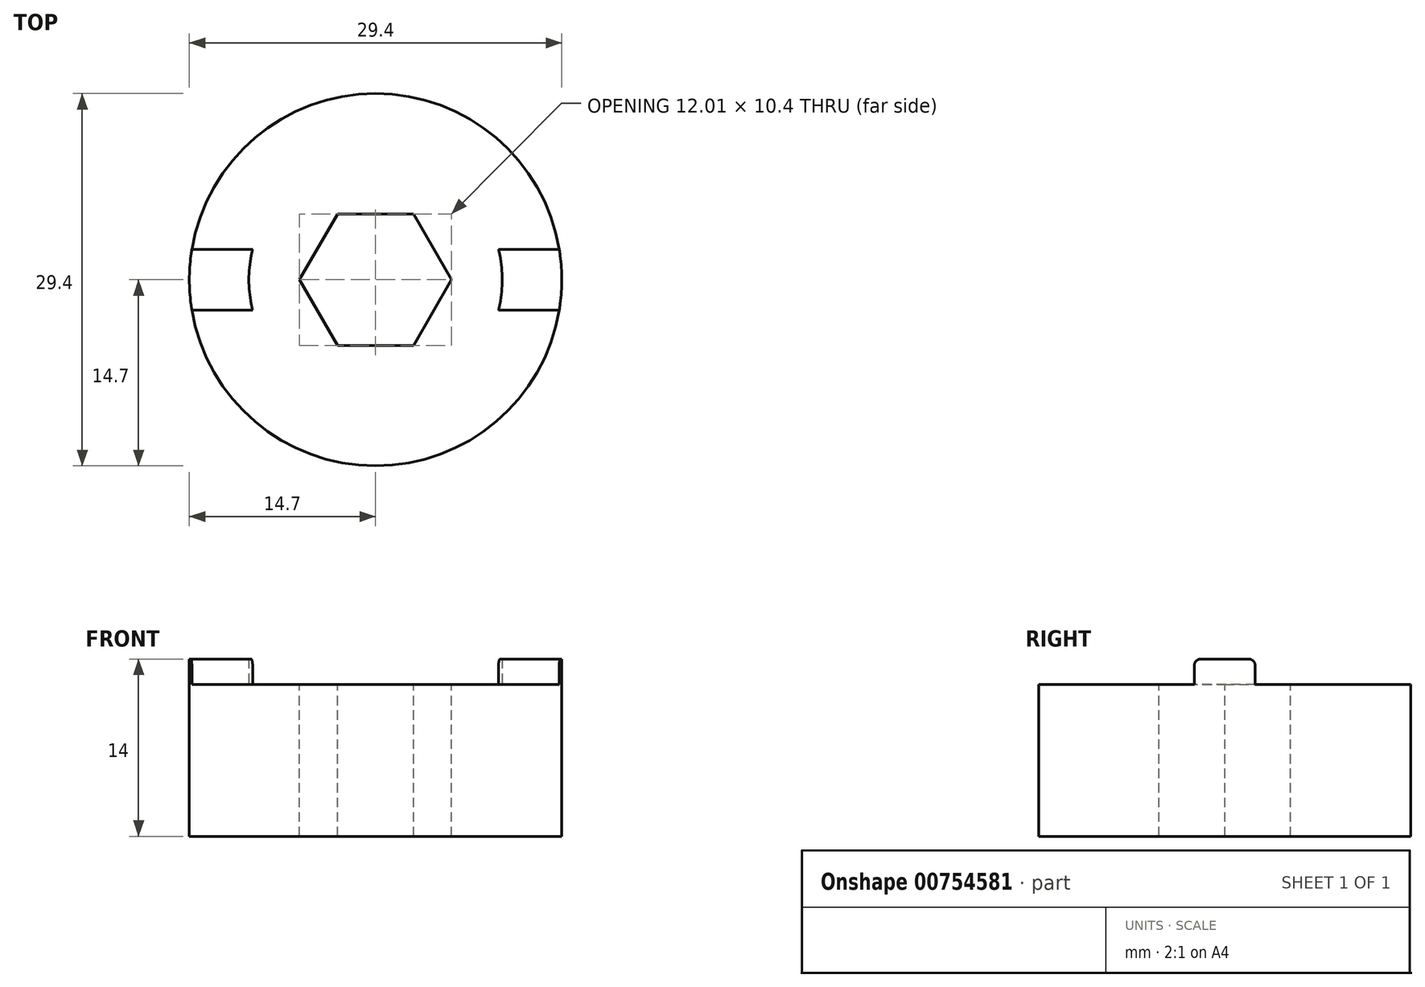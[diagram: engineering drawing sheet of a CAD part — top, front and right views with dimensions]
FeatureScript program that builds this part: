
annotation { "Feature Type Name" : "Feature", "Feature Type Description" : "" }
export const myFeature = defineFeature(function(context is Context, id is Id, definition is map)
    precondition{}
    {
        {
            var Q0;
            Q0=qCreatedBy(makeId("Top.planeOp"),FACE);
            var sketch = newSketch(context, id + "F0", { "sketchPlane" : qUnion([Q0])});
            skCircle(sketch, "E0", {"center": v(0, 0) * mm, "radius": 14.7 * mm});
            skSolve(sketch);
        }
        {
            var Q0;
            Q0 = qSketchRegion(id + "F0", true);
            extrude(context, id + "F1", {"entities" : qUnion([Q0]), "depth" : 24 * mm, "offsetDistance" : 25 * mm});
        }
        {
            var Q0;
            Q0=makeQuery(id+"F1.opExtrude","CAP_FACE",FACE,{"disambiguationData":[OSD([sQuery(id+"F0.wireOp",EDGE,"E0")])],"isStart":false});
            var sketch = newSketch(context, id + "F2", { "sketchPlane" : qUnion([Q0])});
            skLineSegment(sketch, "E1.bottom", {"start": v(14.5, 2.4) * mm, "end": v(-14.5, 2.4) * mm});
            skLineSegment(sketch, "E1.top", {"start": v(14.5, -2.4) * mm, "end": v(-14.5, -2.4) * mm});
            skPoint(sketch, "E1.middle", {"position": v(0, 0) * mm});
            skArc(sketch, "E2.0", {"start": v(14.5, -2.4) * mm, "mid": v(14.7, 0) * mm, "end": v(14.5, 2.4) * mm});
            skArc(sketch, "E3.trimOffspring", {"start": v(-14.5, 2.4) * mm, "mid": v(-14.7, 0) * mm, "end": v(-14.5, -2.4) * mm});
            skLineSegment(sketch, "E4", {"start": v(-14.7, 0) * mm, "end": v(14.7, 0) * mm, "construction": true});
            skSolve(sketch);
        }
        {
            var Q0;
            Q0 = qSketchRegion(id + "F2", true);
            extrude(context, id + "F3", {"entities" : qUnion([Q0]), "operationType" : NewBodyOperationType.ADD, "depth" : 2 * mm, "offsetDistance" : 25 * mm});
        }
        {
            var Q0;
            {var subQ0=sQuery(id+"F0.wireOp",EDGE,"E0");Q0=makeQuery(id+"F3.boolean.opBoolean","SPLIT",FACE,{"disambiguationData":[TD([makeQuery(id+"F3.opExtrude","SWEPT_FACE",FACE,{"disambiguationData":[OSD([sQuery(id+"F2.wireOp",EDGE,"E1.top")])]})])],"derivedFrom":makeQuery(id+"F1.opExtrude","CAP_FACE",FACE,{"disambiguationData":[OSD([subQ0])],"isStart":false})});}
            var sketch = newSketch(context, id + "F4", { "sketchPlane" : qUnion([Q0])});
            skCircle(sketch, "E5", {"center": v(0, 0) * mm, "radius": 10 * mm});
            skSolve(sketch);
        }
        {
            var Q0;
            Q0 = qSketchRegion(id + "F4", true);
            extrude(context, id + "F5", {"entities" : qUnion([Q0]), "operationType" : NewBodyOperationType.REMOVE, "endBound" : BoundingType.THROUGH_ALL, "depth" : 25 * mm, "offsetDistance" : 25 * mm});
        }
        {
            var Q0;
            {var subQ0=sQuery(id+"F0.wireOp",EDGE,"E0");var subQ4=makeQuery(id+"F1.opExtrude","CAP_FACE",FACE,{"disambiguationData":[OSD([subQ0])],"isStart":false});Q0=makeQuery(id+"F5.boolean.opBoolean","MERGE",FACE,{"derivedFrom":[makeQuery(id+"F3.boolean.opBoolean","SPLIT",FACE,{"disambiguationData":[TD([makeQuery(id+"F3.opExtrude","SWEPT_FACE",FACE,{"disambiguationData":[OSD([sQuery(id+"F2.wireOp",EDGE,"E1.bottom")])]})])],"derivedFrom":subQ4}),makeQuery(id+"F3.boolean.opBoolean","SPLIT",FACE,{"disambiguationData":[TD([makeQuery(id+"F3.opExtrude","SWEPT_FACE",FACE,{"disambiguationData":[OSD([sQuery(id+"F2.wireOp",EDGE,"E1.top")])]})])],"derivedFrom":subQ4}),makeQuery(id+"F5.opExtrude","CAP_FACE",FACE,{"disambiguationData":[OSD([sQuery(id+"F4.wireOp",EDGE,"E5")])],"isStart":true})]});}
            var sketch = newSketch(context, id + "F6", { "sketchPlane" : qUnion([Q0])});
            skCircle(sketch, "E6.cCircle", {"center": v(0, 0) * mm, "radius": 5.2 * mm, "construction": true});
            skLineSegment(sketch, "E6.0", {"start": v(-3, 5.2) * mm, "end": v(3, 5.2) * mm});
            skLineSegment(sketch, "E6.1", {"start": v(3, 5.2) * mm, "end": v(6, 0) * mm});
            skLineSegment(sketch, "E6.2", {"start": v(6, 0) * mm, "end": v(3, -5.2) * mm});
            skLineSegment(sketch, "E6.3", {"start": v(3, -5.2) * mm, "end": v(-3, -5.2) * mm});
            skLineSegment(sketch, "E6.4", {"start": v(-3, -5.2) * mm, "end": v(-6, 0) * mm});
            skLineSegment(sketch, "E6.5", {"start": v(-6, 0) * mm, "end": v(-3, 5.2) * mm});
            skPoint(sketch, "E6.0.midPoint", {"position": v(0, 5.2) * mm});
            skSolve(sketch);
        }
        {
            var Q0;
            Q0 = qSketchRegion(id + "F6", true);
            extrude(context, id + "F7", {"entities" : qUnion([Q0]), "operationType" : NewBodyOperationType.REMOVE, "endBound" : BoundingType.THROUGH_ALL, "oppositeDirection" : true, "depth" : 25 * mm, "offsetDistance" : 25 * mm});
        }
        {
            var Q0;
            Q0=makeQuery(id+"F1.opExtrude","CAP_FACE",FACE,{"disambiguationData":[OSD([sQuery(id+"F0.wireOp",EDGE,"E0")])],"isStart":true});
            var sketch = newSketch(context, id + "F8", { "sketchPlane" : qUnion([Q0])});
            skCircle(sketch, "E7.cCircle", {"center": v(0, 0) * mm, "radius": 9.45 * mm, "construction": true});
            skLineSegment(sketch, "E7.0", {"start": v(10.91, 0) * mm, "end": v(5.46, -9.45) * mm});
            skLineSegment(sketch, "E7.1", {"start": v(5.46, -9.45) * mm, "end": v(-5.46, -9.45) * mm});
            skLineSegment(sketch, "E7.2", {"start": v(-5.46, -9.45) * mm, "end": v(-10.91, 0) * mm});
            skLineSegment(sketch, "E7.3", {"start": v(-10.91, 0) * mm, "end": v(-5.46, 9.45) * mm});
            skLineSegment(sketch, "E7.4", {"start": v(-5.46, 9.45) * mm, "end": v(5.46, 9.45) * mm});
            skLineSegment(sketch, "E7.5", {"start": v(5.46, 9.45) * mm, "end": v(10.91, 0) * mm});
            skPoint(sketch, "E7.0.midPoint", {"position": v(8.18, -4.72) * mm});
            skCircle(sketch, "E8.0", {"center": v(0, 0) * mm, "radius": 14.7 * mm});
            skSolve(sketch);
        }
        {
            var Q0;
            Q0 = qSketchRegion(id + "F8", true);
            extrude(context, id + "F9", {"entities" : qUnion([Q0]), "operationType" : NewBodyOperationType.REMOVE, "oppositeDirection" : true, "depth" : 12 * mm, "offsetDistance" : 25 * mm});
        }
        {
            var Q0;
            Q0=makeQuery(id+"F9.boolean.opBoolean","COPY",EDGE,{"derivedFrom":makeQuery(id+"F9.opExtrude","CAP_EDGE",EDGE,{"disambiguationData":[OSD([sQuery(id+"F8.wireOp",EDGE,"E7.1")])],"isStart":false})});
            var Q1;
            Q1=makeQuery(id+"F9.boolean.opBoolean","COPY",EDGE,{"derivedFrom":makeQuery(id+"F9.opExtrude","CAP_EDGE",EDGE,{"disambiguationData":[OSD([sQuery(id+"F8.wireOp",EDGE,"E7.0")])],"isStart":false})});
            var Q2;
            Q2=makeQuery(id+"F9.boolean.opBoolean","COPY",EDGE,{"derivedFrom":makeQuery(id+"F9.opExtrude","CAP_EDGE",EDGE,{"disambiguationData":[OSD([sQuery(id+"F8.wireOp",EDGE,"E7.5")])],"isStart":false})});
            var Q3;
            Q3=makeQuery(id+"F9.boolean.opBoolean","COPY",EDGE,{"derivedFrom":makeQuery(id+"F9.opExtrude","CAP_EDGE",EDGE,{"disambiguationData":[OSD([sQuery(id+"F8.wireOp",EDGE,"E7.4")])],"isStart":false})});
            var Q4;
            Q4=makeQuery(id+"F9.boolean.opBoolean","COPY",EDGE,{"derivedFrom":makeQuery(id+"F9.opExtrude","CAP_EDGE",EDGE,{"disambiguationData":[OSD([sQuery(id+"F8.wireOp",EDGE,"E7.3")])],"isStart":false})});
            var Q5;
            Q5=makeQuery(id+"F9.boolean.opBoolean","COPY",EDGE,{"derivedFrom":makeQuery(id+"F9.opExtrude","CAP_EDGE",EDGE,{"disambiguationData":[OSD([sQuery(id+"F8.wireOp",EDGE,"E7.2")])],"isStart":false})});
            var Q6;
            Q6=makeQuery(id+"F5.boolean.opBoolean","SPLIT",EDGE,{"disambiguationData":[OD(1.0)],"derivedFrom":makeQuery(id+"F3.opExtrude","CAP_EDGE",EDGE,{"disambiguationData":[OSD([sQuery(id+"F2.wireOp",EDGE,"E1.bottom")])],"isStart":false})});
            var Q7;
            Q7=makeQuery(id+"F5.boolean.opBoolean","SPLIT",EDGE,{"disambiguationData":[OD(1.0)],"derivedFrom":makeQuery(id+"F3.opExtrude","CAP_EDGE",EDGE,{"disambiguationData":[OSD([sQuery(id+"F2.wireOp",EDGE,"E1.top")])],"isStart":false})});
            var Q8;
            Q8=makeQuery(id+"F5.boolean.opBoolean","SPLIT",EDGE,{"disambiguationData":[OD(0.0)],"derivedFrom":makeQuery(id+"F3.opExtrude","CAP_EDGE",EDGE,{"disambiguationData":[OSD([sQuery(id+"F2.wireOp",EDGE,"E1.top")])],"isStart":false})});
            var Q9;
            Q9=makeQuery(id+"F5.boolean.opBoolean","SPLIT",EDGE,{"disambiguationData":[OD(0.0)],"derivedFrom":makeQuery(id+"F3.opExtrude","CAP_EDGE",EDGE,{"disambiguationData":[OSD([sQuery(id+"F2.wireOp",EDGE,"E1.bottom")])],"isStart":false})});
            fillet(context, id + "F10", {"entities" : qUnion([Q0, Q1, Q2, Q3, Q4, Q5, Q6, Q7, Q8, Q9]), "radius" : .5 * mm, "tangentPropagation" : true, "allowEdgeOverflow" : false});
        }
        {
            var Q0;
            Q0=makeQuery(id+"F1.opExtrude","CAP_FACE",FACE,{"disambiguationData":[OSD([sQuery(id+"F0.wireOp",EDGE,"E0")])],"isStart":true});
            var sketch = newSketch(context, id + "F11", { "sketchPlane" : qUnion([Q0])});
            skCircle(sketch, "E9", {"center": v(0, 0) * mm, "radius": 18.99 * mm});
            skSolve(sketch);
        }
        {
            var Q0;
            Q0 = qSketchRegion(id + "F11", true);
            var Q1;
            Q1=makeQuery(id+"F9.boolean.opBoolean","COPY",FACE,{"derivedFrom":makeQuery(id+"F9.opExtrude","CAP_FACE",FACE,{"disambiguationData":[OSD([sQuery(id+"F8.wireOp",EDGE,"E7.0"),sQuery(id+"F8.wireOp",EDGE,"E7.1"),sQuery(id+"F8.wireOp",EDGE,"E7.2"),sQuery(id+"F8.wireOp",EDGE,"E7.3"),sQuery(id+"F8.wireOp",EDGE,"E7.4"),sQuery(id+"F8.wireOp",EDGE,"E7.5"),sQuery(id+"F8.wireOp",EDGE,"E8.0")])],"isStart":false})});
            extrude(context, id + "F12", {"entities" : qUnion([Q0]), "operationType" : NewBodyOperationType.REMOVE, "endBound" : BoundingType.UP_TO_SURFACE, "oppositeDirection" : true, "depth" : 25 * mm, "endBoundEntityFace" : qUnion([Q1]), "offsetDistance" : 25 * mm});
        }
    });
